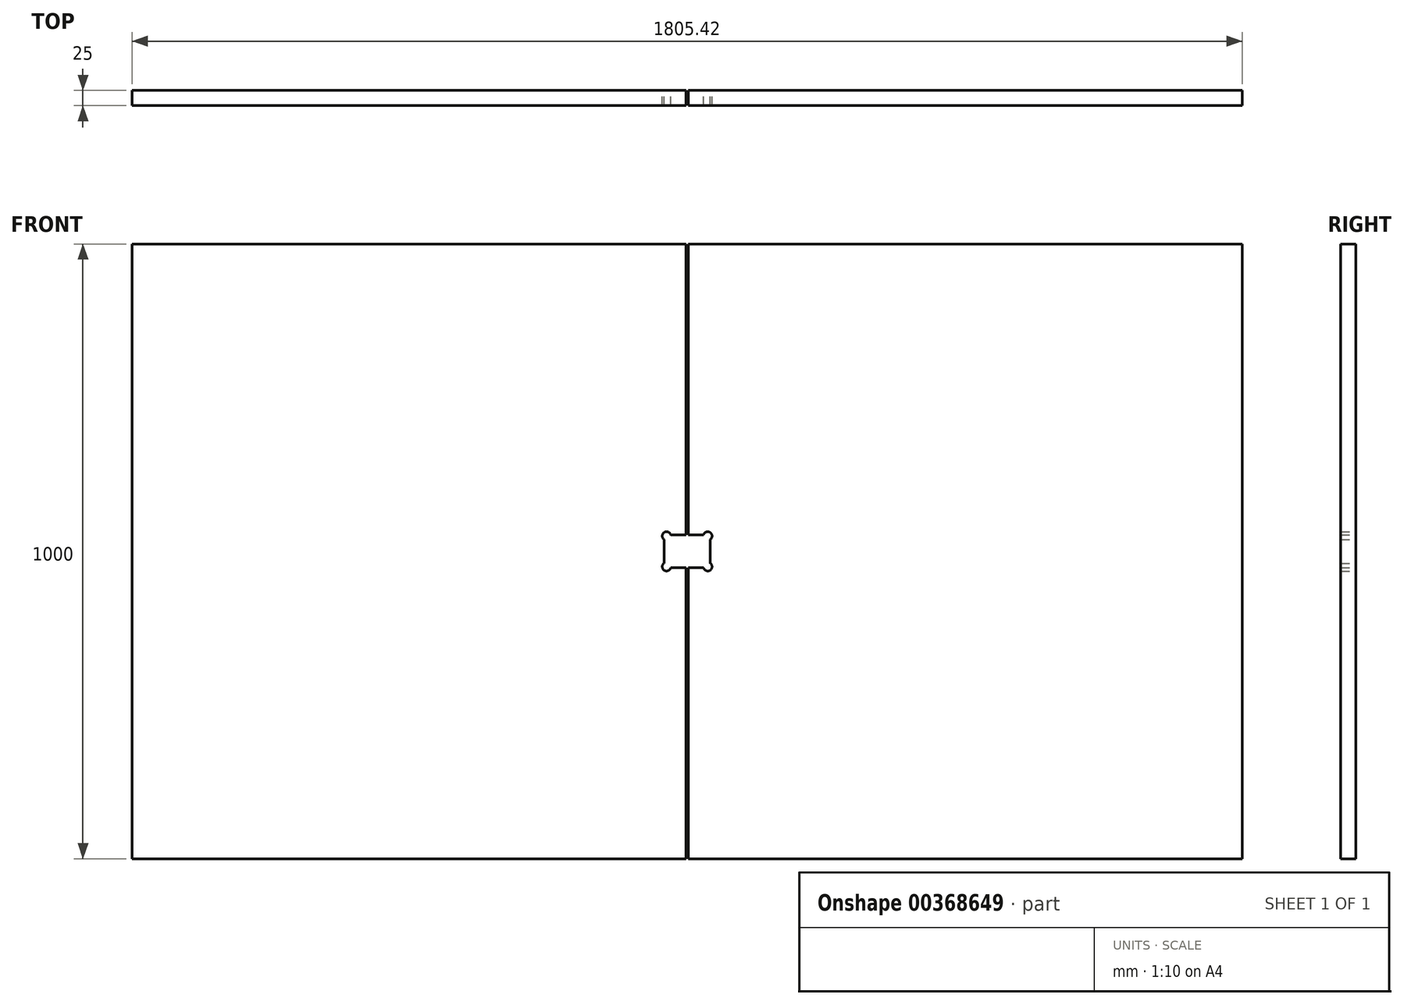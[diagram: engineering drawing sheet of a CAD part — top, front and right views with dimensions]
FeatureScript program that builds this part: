
annotation { "Feature Type Name" : "Feature", "Feature Type Description" : "" }
export const myFeature = defineFeature(function(context is Context, id is Id, definition is map)
    precondition{}
    {
        {
            var Q0;
            Q0=qCreatedBy(makeId("Front.planeOp"),FACE);
            var sketch = newSketch(context, id + "F0", { "sketchPlane" : qUnion([Q0])});
            skLineSegment(sketch, "E0", {"start": v(0, 500) * mm, "end": v(0, 26.5) * mm});
            skLineSegment(sketch, "E1", {"start": v(0, 26.5) * mm, "end": v(24.66, 26.5) * mm});
            skArc(sketch, "E2", {"start": v(35.5, 19.26) * mm, "mid": v(35.4, 30.82) * mm, "end": v(24.66, 26.5) * mm});
            skLineSegment(sketch, "E3", {"start": v(35.5, 19.26) * mm, "end": v(35.5, -19.26) * mm});
            skArc(sketch, "E4", {"start": v(24.66, -26.5) * mm, "mid": v(35.4, -30.82) * mm, "end": v(35.5, -19.26) * mm});
            skLineSegment(sketch, "E5", {"start": v(24.66, -26.5) * mm, "end": v(0, -26.5) * mm});
            skLineSegment(sketch, "E6", {"start": v(0, -26.5) * mm, "end": v(0, -500) * mm});
            skLineSegment(sketch, "E7", {"start": v(0, 500) * mm, "end": v(900.71, 500) * mm});
            skLineSegment(sketch, "E8", {"start": v(900.71, 500) * mm, "end": v(900.71, -500) * mm});
            skLineSegment(sketch, "E9", {"start": v(900.71, -500) * mm, "end": v(0, -500) * mm});
            skSolve(sketch);
        }
        {
            var Q0;
            Q0=qSketchRegion(id+"F0",true);
            extrude(context, id + "F1", {"entities" : qUnion([Q0]), "depth" : 25 * mm});
        }
        {
            var Q0;
            Q0=makeQuery(id+"F1.opExtrude","SWEPT_FACE",FACE,{"disambiguationData":[OSD([sQuery(id+"F0.wireOp",EDGE,"E0")])]});
            cPlane(context, id + "F2", {"entities" : qUnion([Q0]), "cplaneType" : CPlaneType.OFFSET, "offset" : 2 * mm, "width" : 150 * mm, "height" : 150 * mm});
        }
        {
            var Q0;
            Q0=makeQuery(id+"F1.opExtrude","SWEPT_BODY",BODY,{"disambiguationData":[OSD([sQuery(id+"F0.wireOp",EDGE,"E0"),sQuery(id+"F0.wireOp",EDGE,"E1"),sQuery(id+"F0.wireOp",EDGE,"E2"),sQuery(id+"F0.wireOp",EDGE,"E3"),sQuery(id+"F0.wireOp",EDGE,"E4"),sQuery(id+"F0.wireOp",EDGE,"E5"),sQuery(id+"F0.wireOp",EDGE,"E6"),sQuery(id+"F0.wireOp",EDGE,"E7"),sQuery(id+"F0.wireOp",EDGE,"E8"),sQuery(id+"F0.wireOp",EDGE,"E9")])]});
            var Q1;
            Q1=qCreatedBy(id+"F2.planeOp",FACE);
            mirror(context, id + "F3", {"entities" : qUnion([Q0]), "mirrorPlane" : qUnion([Q1])});
        }
    });
